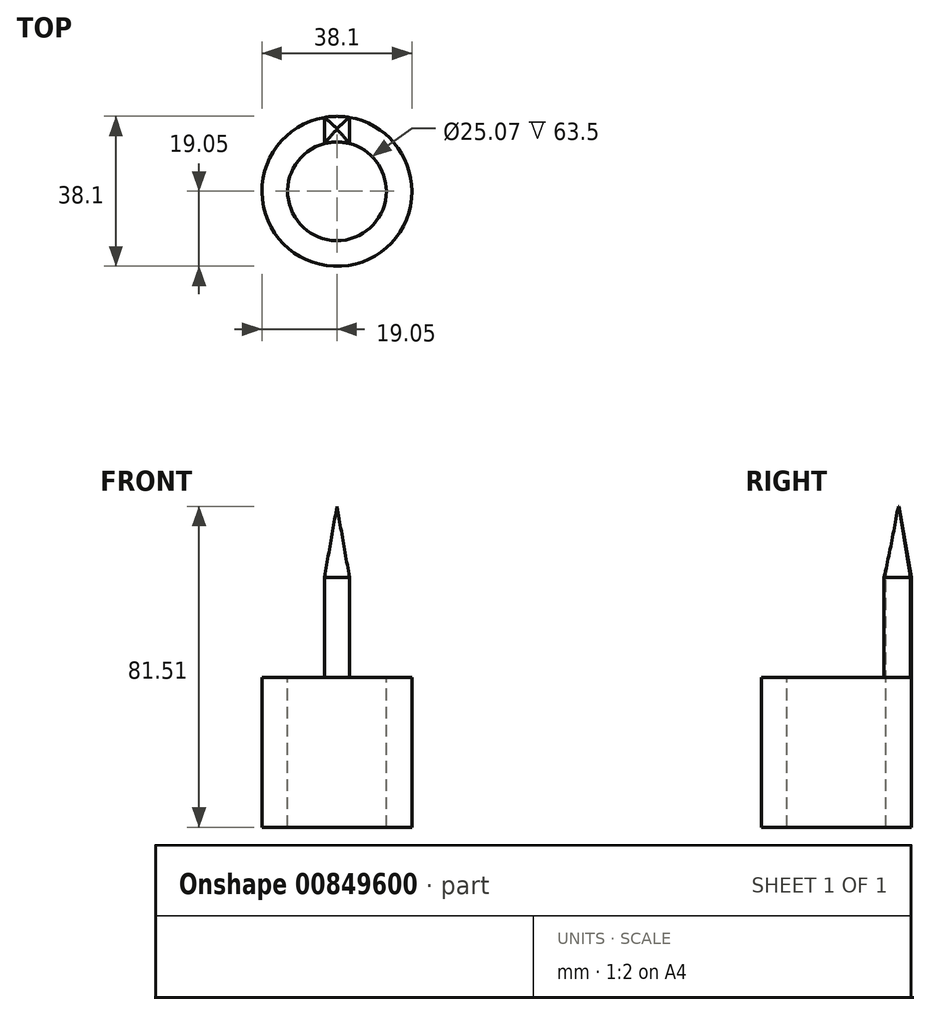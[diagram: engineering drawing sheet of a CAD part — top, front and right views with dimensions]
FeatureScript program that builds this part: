
annotation { "Feature Type Name" : "Feature", "Feature Type Description" : "" }
export const myFeature = defineFeature(function(context is Context, id is Id, definition is map)
    precondition{}
    {
        {
            var Q0;
            Q0=qCreatedBy(makeId("Top.planeOp"),FACE);
            var sketch = newSketch(context, id + "F0", { "sketchPlane" : qUnion([Q0])});
            skCircle(sketch, "E0", {"center": v(0, 0) * mm, "radius": 19.05 * mm});
            skSolve(sketch);
        }
        {
            var Q0;
            Q0=makeQuery(id+"F0.imprint","IMPRINT",FACE,{"disambiguationData":[TD([[makeQuery(id+"F0.imprint","IMPRINT",EDGE,{"derivedFrom":sQuery(id+"F0.wireOp",EDGE,"E0")}),1.0]])]});
            extrude(context, id + "F1", {"entities" : qUnion([Q0]), "oppositeDirection" : true, "depth" : 63.5 * mm, "offsetDistance" : 25.4 * mm});
        }
        {
            var Q0;
            Q0=makeQuery(id+"F1.opExtrude","CAP_FACE",FACE,{"disambiguationData":[OSD([sQuery(id+"F0.wireOp",EDGE,"E0")])],"isStart":true});
            var sketch = newSketch(context, id + "F2", { "sketchPlane" : qUnion([Q0])});
            skPoint(sketch, "E1", {"position": v(0, 0) * mm});
            skSolve(sketch);
        }
        {
            var Q0;
            Q0=sQuery(id+"F2.wireOp",VERTEX,"E1");
            var Q1;
            Q1=makeQuery(id+"F1.opExtrude","SWEPT_BODY",BODY,{"disambiguationData":[OSD([sQuery(id+"F0.wireOp",EDGE,"E0")])]});
            hole(context, id + "F3", {"style" : HoleStyle.SIMPLE, "endStyle" : HoleEndStyle.THROUGH, "holeDiameter" : 25.07 * mm, "majorDiameter" : 19.05 * mm, "isTappedThrough" : true, "tappedDepth" : 25.41 * mm, "tapClearance" : 3, "locations" : qUnion([Q0]), "scope" : qUnion([Q1])});
        }
        {
            var Q0;
            Q0=makeQuery(id+"F1.opExtrude","CAP_FACE",FACE,{"disambiguationData":[OSD([sQuery(id+"F0.wireOp",EDGE,"E0")])],"isStart":true});
            var sketch = newSketch(context, id + "F4", { "sketchPlane" : qUnion([Q0])});
            skLineSegment(sketch, "E2.bottom", {"start": v(-3.18, 28.8) * mm, "end": v(3.18, 28.8) * mm});
            skLineSegment(sketch, "E2.top", {"start": v(-3.18, -28.8) * mm, "end": v(3.18, -28.8) * mm});
            skLineSegment(sketch, "E2.left", {"start": v(-3.18, 28.8) * mm, "end": v(-3.18, -28.8) * mm});
            skLineSegment(sketch, "E2.right", {"start": v(3.18, 28.8) * mm, "end": v(3.18, -28.8) * mm});
            skPoint(sketch, "E2.middle", {"position": v(0, 0) * mm});
            skSolve(sketch);
        }
        {
            var Q0;
            {var subQ0=sQuery(id+"F4.wireOp",EDGE,"E2.left");var subQ1=makeQuery(id+"F1.opExtrude","CAP_EDGE",EDGE,{"disambiguationData":[OSD([sQuery(id+"F0.wireOp",EDGE,"E0")])],"isStart":true});var subQ2=makeQuery(id+"F4.imprint","INTERSECT",VERTEX,{"disambiguationData":[OD(0.0)],"derivedFrom":[subQ1,subQ0]});Q0=makeQuery(id+"F4.imprint","IMPRINT",FACE,{"disambiguationData":[TD([[makeQuery(id+"F4.imprint","IMPRINT",EDGE,{"disambiguationData":[TD([[subQ2,1.0]])],"derivedFrom":subQ1}),1.0]])]});}
            extrude(context, id + "F5", {"entities" : qUnion([Q0]), "operationType" : NewBodyOperationType.ADD, "depth" : 50.8 * mm, "offsetDistance" : 25.4 * mm, "hasDraft" : true, "draftAngle" : 10 * degree, "draftPullDirection" : true});
        }
        {
            var Q0;
            {var subQ0=sQuery(id+"F0.wireOp",EDGE,"E0");var subQ2=sQuery(id+"F4.wireOp",EDGE,"E2.right");var subQ3=makeQuery(id+"FMHHlkISV1QRiGu_1.5.F5.opExtrude","SWEPT_FACE",FACE,{"disambiguationData":[OSD([subQ2])]});var subQ9=sQuery(id+"F4.wireOp",EDGE,"E2.left");var subQ11=makeQuery(id+"F5.opExtrude","SWEPT_FACE",FACE,{"disambiguationData":[OSD([subQ9])]});Q0=makeQuery(id+"FMHHlkISV1QRiGu_1.6.F5.boolean.opBoolean","SPLIT",FACE,{"disambiguationData":[TD([subQ3])],"derivedFrom":makeQuery(id+"FMHHlkISV1QRiGu_1.5.F5.boolean.opBoolean","SPLIT",FACE,{"disambiguationData":[TD([subQ11])],"derivedFrom":makeQuery(id+"FMHHlkISV1QRiGu_1.4.F5.boolean.opBoolean","SPLIT",FACE,{"disambiguationData":[TD([subQ11])],"derivedFrom":makeQuery(id+"FMHHlkISV1QRiGu_1.3.F5.boolean.opBoolean","SPLIT",FACE,{"disambiguationData":[TD([subQ11])],"derivedFrom":makeQuery(id+"FMHHlkISV1QRiGu_1.2.F5.boolean.opBoolean","SPLIT",FACE,{"disambiguationData":[TD([subQ11])],"derivedFrom":makeQuery(id+"FMHHlkISV1QRiGu_1.1.F5.boolean.opBoolean","SPLIT",FACE,{"disambiguationData":[TD([subQ11])],"derivedFrom":makeQuery(id+"F1.opExtrude","CAP_FACE",FACE,{"disambiguationData":[OSD([subQ0])],"isStart":true})})})})})})});}
            var Q1;
            {var subQ0=sQuery(id+"F0.wireOp",EDGE,"E0");var subQ2=sQuery(id+"F4.wireOp",EDGE,"E2.right");var subQ3=makeQuery(id+"FMHHlkISV1QRiGu_1.4.F5.opExtrude","SWEPT_FACE",FACE,{"disambiguationData":[OSD([subQ2])]});var subQ9=sQuery(id+"F4.wireOp",EDGE,"E2.left");var subQ11=makeQuery(id+"F5.opExtrude","SWEPT_FACE",FACE,{"disambiguationData":[OSD([subQ9])]});Q1=makeQuery(id+"FMHHlkISV1QRiGu_1.5.F5.boolean.opBoolean","SPLIT",FACE,{"disambiguationData":[TD([subQ3])],"derivedFrom":makeQuery(id+"FMHHlkISV1QRiGu_1.4.F5.boolean.opBoolean","SPLIT",FACE,{"disambiguationData":[TD([subQ11])],"derivedFrom":makeQuery(id+"FMHHlkISV1QRiGu_1.3.F5.boolean.opBoolean","SPLIT",FACE,{"disambiguationData":[TD([subQ11])],"derivedFrom":makeQuery(id+"FMHHlkISV1QRiGu_1.2.F5.boolean.opBoolean","SPLIT",FACE,{"disambiguationData":[TD([subQ11])],"derivedFrom":makeQuery(id+"FMHHlkISV1QRiGu_1.1.F5.boolean.opBoolean","SPLIT",FACE,{"disambiguationData":[TD([subQ11])],"derivedFrom":makeQuery(id+"F1.opExtrude","CAP_FACE",FACE,{"disambiguationData":[OSD([subQ0])],"isStart":true})})})})})});}
            var Q2;
            {var subQ0=sQuery(id+"F0.wireOp",EDGE,"E0");var subQ2=sQuery(id+"F4.wireOp",EDGE,"E2.right");var subQ3=makeQuery(id+"FMHHlkISV1QRiGu_1.3.F5.opExtrude","SWEPT_FACE",FACE,{"disambiguationData":[OSD([subQ2])]});var subQ9=sQuery(id+"F4.wireOp",EDGE,"E2.left");var subQ11=makeQuery(id+"F5.opExtrude","SWEPT_FACE",FACE,{"disambiguationData":[OSD([subQ9])]});Q2=makeQuery(id+"FMHHlkISV1QRiGu_1.4.F5.boolean.opBoolean","SPLIT",FACE,{"disambiguationData":[TD([subQ3])],"derivedFrom":makeQuery(id+"FMHHlkISV1QRiGu_1.3.F5.boolean.opBoolean","SPLIT",FACE,{"disambiguationData":[TD([subQ11])],"derivedFrom":makeQuery(id+"FMHHlkISV1QRiGu_1.2.F5.boolean.opBoolean","SPLIT",FACE,{"disambiguationData":[TD([subQ11])],"derivedFrom":makeQuery(id+"FMHHlkISV1QRiGu_1.1.F5.boolean.opBoolean","SPLIT",FACE,{"disambiguationData":[TD([subQ11])],"derivedFrom":makeQuery(id+"F1.opExtrude","CAP_FACE",FACE,{"disambiguationData":[OSD([subQ0])],"isStart":true})})})})});}
            var Q3;
            {var subQ0=sQuery(id+"F0.wireOp",EDGE,"E0");var subQ2=sQuery(id+"F4.wireOp",EDGE,"E2.right");var subQ3=makeQuery(id+"FMHHlkISV1QRiGu_1.2.F5.opExtrude","SWEPT_FACE",FACE,{"disambiguationData":[OSD([subQ2])]});var subQ9=sQuery(id+"F4.wireOp",EDGE,"E2.left");var subQ11=makeQuery(id+"F5.opExtrude","SWEPT_FACE",FACE,{"disambiguationData":[OSD([subQ9])]});Q3=makeQuery(id+"FMHHlkISV1QRiGu_1.3.F5.boolean.opBoolean","SPLIT",FACE,{"disambiguationData":[TD([subQ3])],"derivedFrom":makeQuery(id+"FMHHlkISV1QRiGu_1.2.F5.boolean.opBoolean","SPLIT",FACE,{"disambiguationData":[TD([subQ11])],"derivedFrom":makeQuery(id+"FMHHlkISV1QRiGu_1.1.F5.boolean.opBoolean","SPLIT",FACE,{"disambiguationData":[TD([subQ11])],"derivedFrom":makeQuery(id+"F1.opExtrude","CAP_FACE",FACE,{"disambiguationData":[OSD([subQ0])],"isStart":true})})})});}
            var Q4;
            {var subQ0=sQuery(id+"F0.wireOp",EDGE,"E0");var subQ2=makeQuery(id+"FMHHlkISV1QRiGu_1.1.F5.opExtrude","SWEPT_FACE",FACE,{"disambiguationData":[OSD([sQuery(id+"F4.wireOp",EDGE,"E2.right")])]});var subQ8=sQuery(id+"F4.wireOp",EDGE,"E2.left");Q4=makeQuery(id+"FMHHlkISV1QRiGu_1.2.F5.boolean.opBoolean","SPLIT",FACE,{"disambiguationData":[TD([subQ2])],"derivedFrom":makeQuery(id+"FMHHlkISV1QRiGu_1.1.F5.boolean.opBoolean","SPLIT",FACE,{"disambiguationData":[TD([makeQuery(id+"F5.opExtrude","SWEPT_FACE",FACE,{"disambiguationData":[OSD([subQ8])]})])],"derivedFrom":makeQuery(id+"F1.opExtrude","CAP_FACE",FACE,{"disambiguationData":[OSD([subQ0])],"isStart":true})})});}
            var Q5;
            {var subQ0=sQuery(id+"F0.wireOp",EDGE,"E0");Q5=makeQuery(id+"FMHHlkISV1QRiGu_1.1.F5.boolean.opBoolean","SPLIT",FACE,{"disambiguationData":[TD([makeQuery(id+"F5.opExtrude","SWEPT_FACE",FACE,{"disambiguationData":[OSD([sQuery(id+"F4.wireOp",EDGE,"E2.right")])]})])],"derivedFrom":makeQuery(id+"F1.opExtrude","CAP_FACE",FACE,{"disambiguationData":[OSD([subQ0])],"isStart":true})});}
            var Q6;
            {var subQ0=sQuery(id+"F0.wireOp",EDGE,"E0");var subQ6=makeQuery(id+"F5.opExtrude","SWEPT_FACE",FACE,{"disambiguationData":[OSD([sQuery(id+"F4.wireOp",EDGE,"E2.left")])]});Q6=makeQuery(id+"FMHHlkISV1QRiGu_1.6.F5.boolean.opBoolean","SPLIT",FACE,{"disambiguationData":[TD([subQ6])],"derivedFrom":makeQuery(id+"FMHHlkISV1QRiGu_1.5.F5.boolean.opBoolean","SPLIT",FACE,{"disambiguationData":[TD([subQ6])],"derivedFrom":makeQuery(id+"FMHHlkISV1QRiGu_1.4.F5.boolean.opBoolean","SPLIT",FACE,{"disambiguationData":[TD([subQ6])],"derivedFrom":makeQuery(id+"FMHHlkISV1QRiGu_1.3.F5.boolean.opBoolean","SPLIT",FACE,{"disambiguationData":[TD([subQ6])],"derivedFrom":makeQuery(id+"FMHHlkISV1QRiGu_1.2.F5.boolean.opBoolean","SPLIT",FACE,{"disambiguationData":[TD([subQ6])],"derivedFrom":makeQuery(id+"FMHHlkISV1QRiGu_1.1.F5.boolean.opBoolean","SPLIT",FACE,{"disambiguationData":[TD([subQ6])],"derivedFrom":makeQuery(id+"F1.opExtrude","CAP_FACE",FACE,{"disambiguationData":[OSD([subQ0])],"isStart":true})})})})})})});}
            extrude(context, id + "F6", {"entities" : qUnion([Q0, Q1, Q2, Q3, Q4, Q5, Q6]), "operationType" : NewBodyOperationType.REMOVE, "oppositeDirection" : true, "depth" : 25.4 * mm, "offsetDistance" : 25.4 * mm});
        }
    });
